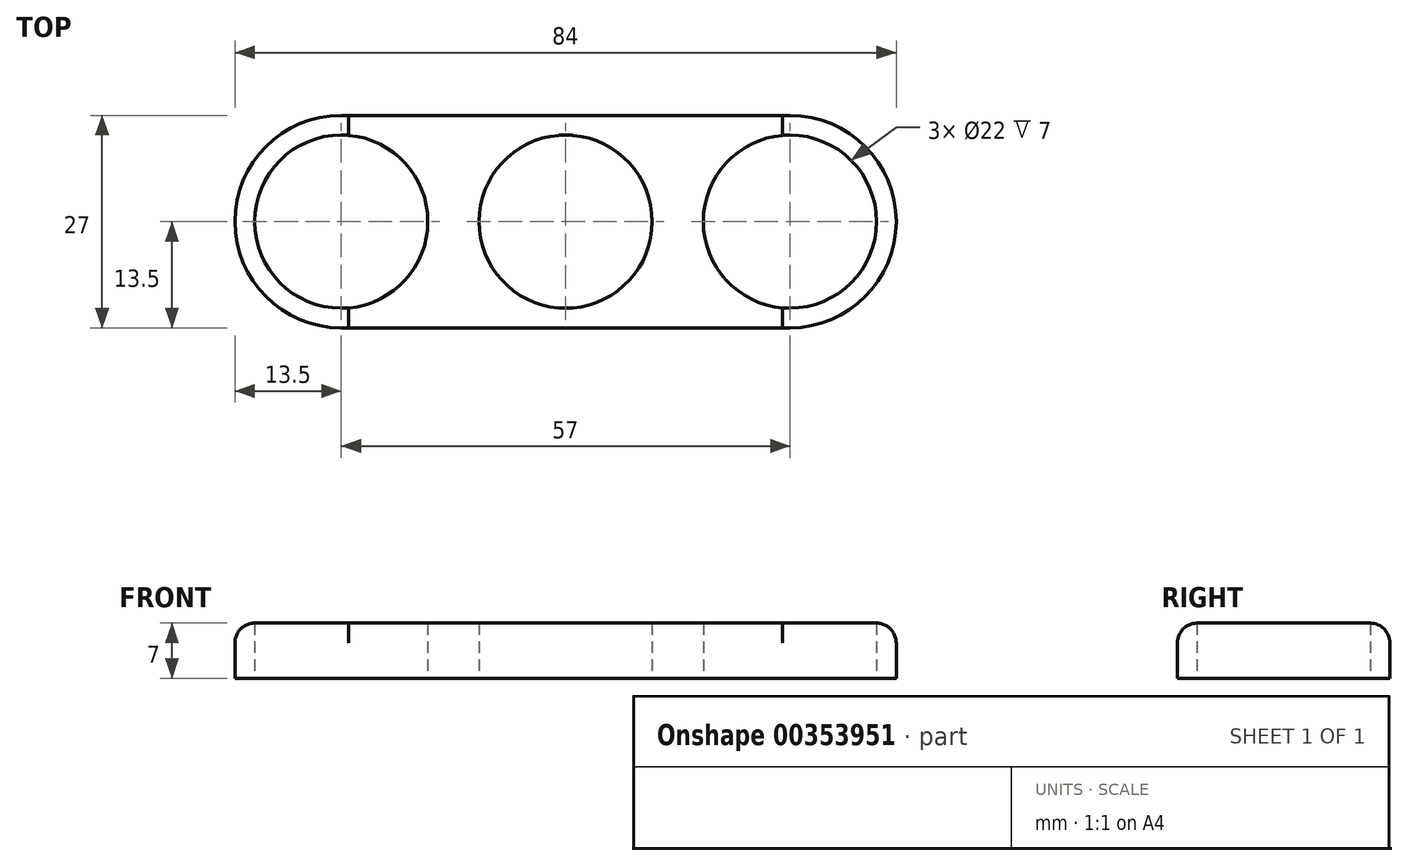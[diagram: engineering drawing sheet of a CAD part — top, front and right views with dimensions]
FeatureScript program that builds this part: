
annotation { "Feature Type Name" : "Feature", "Feature Type Description" : "" }
export const myFeature = defineFeature(function(context is Context, id is Id, definition is map)
    precondition{}
    {
        {
            var Q0;
            Q0=qCreatedBy(makeId("Top.planeOp"),FACE);
            var sketch = newSketch(context, id + "F0", { "sketchPlane" : qUnion([Q0])});
            skCircle(sketch, "E0", {"center": v(-28.5, 0) * mm, "radius": 11 * mm});
            skCircle(sketch, "E1", {"center": v(28.5, 0) * mm, "radius": 11 * mm});
            skCircle(sketch, "E2", {"center": v(-28.5, 0) * mm, "radius": 13.5 * mm});
            skCircle(sketch, "E3", {"center": v(28.5, 0) * mm, "radius": 13.5 * mm});
            skCircle(sketch, "E4", {"center": v(0, 0) * mm, "radius": 11 * mm});
            skLineSegment(sketch, "E5", {"start": v(-28.5, 13.5) * mm, "end": v(28.5, 13.5) * mm});
            skLineSegment(sketch, "E6", {"start": v(-28.5, -13.5) * mm, "end": v(28.5, -13.5) * mm});
            skSolve(sketch);
        }
        {
            var Q0;
            Q0=makeQuery(id+"F0.imprint","IMPRINT",FACE,{"disambiguationData":[TD([[makeQuery(id+"F0.imprint","IMPRINT",EDGE,{"derivedFrom":sQuery(id+"F0.wireOp",EDGE,"E4")}),-1.0]])]});
            var Q1;
            Q1=makeQuery(id+"F0.imprint","IMPRINT",FACE,{"disambiguationData":[TD([[makeQuery(id+"F0.imprint","IMPRINT",EDGE,{"derivedFrom":sQuery(id+"F0.wireOp",EDGE,"E0")}),-1.0]])]});
            var Q2;
            Q2=makeQuery(id+"F0.imprint","IMPRINT",FACE,{"disambiguationData":[TD([[makeQuery(id+"F0.imprint","IMPRINT",EDGE,{"derivedFrom":sQuery(id+"F0.wireOp",EDGE,"E1")}),-1.0]])]});
            extrude(context, id + "F1", {"entities" : qUnion([Q0, Q1, Q2]), "depth" : 7 * mm});
        }
        {
            var Q0;
            Q0=makeQuery(id+"F1.opExtrude","CAP_EDGE",EDGE,{"disambiguationData":[OSD([sQuery(id+"F0.wireOp",EDGE,"E5")])],"isStart":false});
            var Q1;
            Q1=makeQuery(id+"F1.opExtrude","CAP_EDGE",EDGE,{"disambiguationData":[OSD([sQuery(id+"F0.wireOp",EDGE,"E2")])],"isStart":false});
            fillet(context, id + "F2", {"entities" : qUnion([Q0, Q1]), "radius" : 2.54 * mm, "tangentPropagation" : true, "allowEdgeOverflow" : false});
        }
    });
